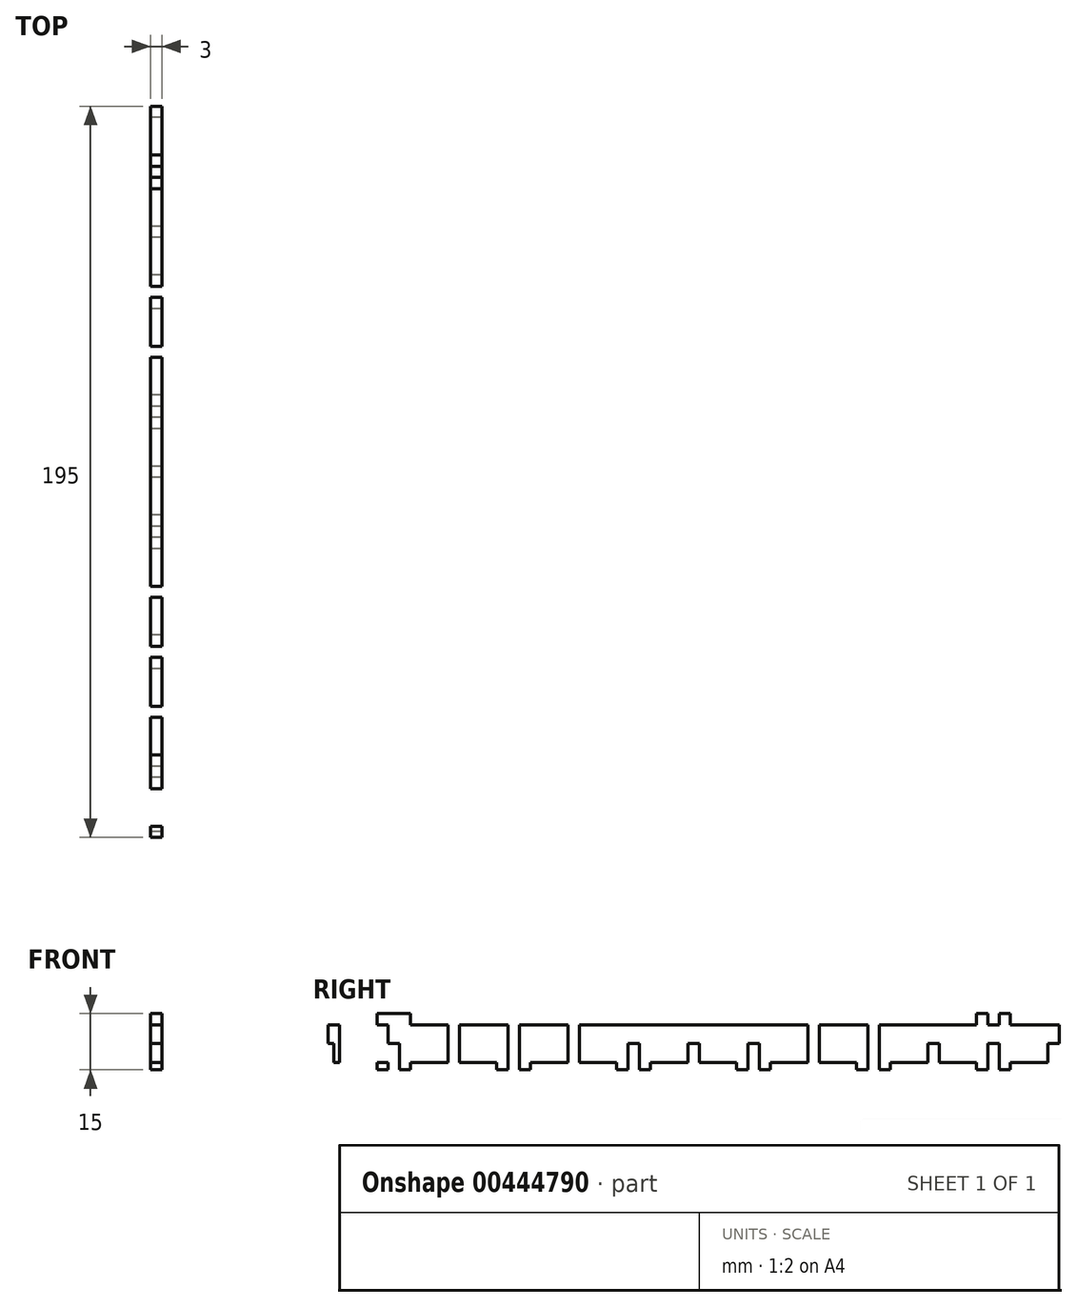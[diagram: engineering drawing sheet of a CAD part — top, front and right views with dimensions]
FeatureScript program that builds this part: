
annotation { "Feature Type Name" : "Feature", "Feature Type Description" : "" }
export const myFeature = defineFeature(function(context is Context, id is Id, definition is map)
    precondition{}
    {
        {
            var Q0;
            Q0=qCreatedBy(makeId("Right.planeOp"),FACE);
            var sketch = newSketch(context, id + "F0", { "sketchPlane" : qUnion([Q0])});
            skLineSegment(sketch, "E0", {"start": v(0, 0) * mm, "end": v(11.5, 0) * mm});
            skLineSegment(sketch, "E1", {"start": v(11.5, 0) * mm, "end": v(11.5, -2) * mm});
            skLineSegment(sketch, "E2", {"start": v(11.5, -2) * mm, "end": v(20.5, -2) * mm});
            skLineSegment(sketch, "E3", {"start": v(20.5, -2) * mm, "end": v(20.5, 0) * mm});
            skLineSegment(sketch, "E4", {"start": v(20.5, 0) * mm, "end": v(43.5, 0) * mm});
            skLineSegment(sketch, "E5", {"start": v(43.5, 0) * mm, "end": v(43.5, -2) * mm});
            skLineSegment(sketch, "E6", {"start": v(43.5, -2) * mm, "end": v(52.5, -2) * mm});
            skLineSegment(sketch, "E7", {"start": v(52.5, -2) * mm, "end": v(52.5, 0) * mm});
            skLineSegment(sketch, "E8", {"start": v(0, 0) * mm, "end": v(0, 10) * mm});
            skPoint(sketch, "E9.oppositeSnap0", {"position": v(0, 5) * mm});
            skLineSegment(sketch, "E9.bottom", {"start": v(0, 10) * mm, "end": v(-1.5, 10) * mm});
            skLineSegment(sketch, "E9.top", {"start": v(0, 5) * mm, "end": v(-1.5, 5) * mm});
            skLineSegment(sketch, "E9.left", {"start": v(0, 10) * mm, "end": v(0, 5) * mm});
            skLineSegment(sketch, "E9.right", {"start": v(-1.5, 10) * mm, "end": v(-1.5, 5) * mm});
            skLineSegment(sketch, "E10.bottom", {"start": v(14.5, 10) * mm, "end": v(17.5, 10) * mm});
            skLineSegment(sketch, "E10.top", {"start": v(14.5, 5) * mm, "end": v(17.5, 5) * mm});
            skLineSegment(sketch, "E10.left", {"start": v(14.5, 10) * mm, "end": v(14.5, 5) * mm});
            skLineSegment(sketch, "E10.right", {"start": v(17.5, 10) * mm, "end": v(17.5, 5) * mm});
            skLineSegment(sketch, "E11.top", {"start": v(0, 0) * mm, "end": v(-1.5, 0) * mm});
            skLineSegment(sketch, "E11.left", {"start": v(0, 5) * mm, "end": v(0, 0) * mm});
            skLineSegment(sketch, "E11.right", {"start": v(-1.5, 5) * mm, "end": v(-1.5, 0) * mm});
            skLineSegment(sketch, "E12.top", {"start": v(14.5, -2) * mm, "end": v(17.5, -2) * mm});
            skLineSegment(sketch, "E12.left", {"start": v(14.5, 5) * mm, "end": v(14.5, -2) * mm});
            skLineSegment(sketch, "E12.right", {"start": v(17.5, 5) * mm, "end": v(17.5, -2) * mm});
            skLineSegment(sketch, "E13.bottom", {"start": v(0, 10) * mm, "end": v(1.5, 10) * mm});
            skLineSegment(sketch, "E13.top", {"start": v(0, 5) * mm, "end": v(1.5, 5) * mm});
            skLineSegment(sketch, "E13.right", {"start": v(1.5, 10) * mm, "end": v(1.5, 5) * mm});
            skLineSegment(sketch, "E14.top", {"start": v(0, 0) * mm, "end": v(1.5, 0) * mm});
            skLineSegment(sketch, "E14.right", {"start": v(1.5, 5) * mm, "end": v(1.5, 0) * mm});
            skLineSegment(sketch, "E15.bottom", {"start": v(11.5, 10) * mm, "end": v(20.5, 10) * mm});
            skLineSegment(sketch, "E15.top", {"start": v(11.5, 13) * mm, "end": v(20.5, 13) * mm});
            skLineSegment(sketch, "E15.left", {"start": v(11.5, 10) * mm, "end": v(11.5, 13) * mm});
            skLineSegment(sketch, "E15.right", {"start": v(20.5, 10) * mm, "end": v(20.5, 13) * mm});
            skLineSegment(sketch, "E16", {"start": v(52.5, 0) * mm, "end": v(75.5, 0) * mm});
            skLineSegment(sketch, "E17", {"start": v(75.5, 0) * mm, "end": v(75.5, -2) * mm});
            skLineSegment(sketch, "E18", {"start": v(75.5, -2) * mm, "end": v(84.5, -2) * mm});
            skLineSegment(sketch, "E19", {"start": v(84.5, -2) * mm, "end": v(84.5, 0) * mm});
            skLineSegment(sketch, "E20", {"start": v(84.5, 0) * mm, "end": v(96, 0) * mm});
            skLineSegment(sketch, "E21", {"start": v(96, 0) * mm, "end": v(96, 19.13) * mm, "construction": true});
            skLineSegment(sketch, "E22", {"start": v(16, 10) * mm, "end": v(16, 11.65) * mm, "construction": true});
            skLineSegment(sketch, "E23.bottom", {"start": v(30.5, 0) * mm, "end": v(33.5, 0) * mm});
            skLineSegment(sketch, "E23.top", {"start": v(30.5, 5) * mm, "end": v(33.5, 5) * mm});
            skLineSegment(sketch, "E23.left", {"start": v(30.5, 0) * mm, "end": v(30.5, 5) * mm});
            skLineSegment(sketch, "E23.right", {"start": v(33.5, 0) * mm, "end": v(33.5, 5) * mm});
            skLineSegment(sketch, "E24.bottom", {"start": v(33.5, 5) * mm, "end": v(30.5, 5) * mm});
            skLineSegment(sketch, "E24.top", {"start": v(33.5, 10) * mm, "end": v(30.5, 10) * mm});
            skLineSegment(sketch, "E24.left", {"start": v(33.5, 5) * mm, "end": v(33.5, 10) * mm});
            skLineSegment(sketch, "E24.right", {"start": v(30.5, 5) * mm, "end": v(30.5, 10) * mm});
            skLineSegment(sketch, "E25", {"start": v(32, 0) * mm, "end": v(32, 2.31) * mm, "construction": true});
            skLineSegment(sketch, "E26.bottom", {"start": v(46.5, -2) * mm, "end": v(49.5, -2) * mm});
            skLineSegment(sketch, "E26.top", {"start": v(46.5, 5) * mm, "end": v(49.5, 5) * mm});
            skLineSegment(sketch, "E26.left", {"start": v(46.5, -2) * mm, "end": v(46.5, 5) * mm});
            skLineSegment(sketch, "E26.right", {"start": v(49.5, -2) * mm, "end": v(49.5, 5) * mm});
            skLineSegment(sketch, "E27.bottom", {"start": v(49.5, 5) * mm, "end": v(46.5, 5) * mm});
            skLineSegment(sketch, "E27.top", {"start": v(49.5, 10) * mm, "end": v(46.5, 10) * mm});
            skLineSegment(sketch, "E27.left", {"start": v(49.5, 5) * mm, "end": v(49.5, 10) * mm});
            skLineSegment(sketch, "E27.right", {"start": v(46.5, 5) * mm, "end": v(46.5, 10) * mm});
            skLineSegment(sketch, "E28.bottom", {"start": v(62.5, 0) * mm, "end": v(65.5, 0) * mm});
            skLineSegment(sketch, "E28.top", {"start": v(62.5, 5) * mm, "end": v(65.5, 5) * mm});
            skLineSegment(sketch, "E28.left", {"start": v(62.5, 0) * mm, "end": v(62.5, 5) * mm});
            skLineSegment(sketch, "E28.right", {"start": v(65.5, 0) * mm, "end": v(65.5, 5) * mm});
            skLineSegment(sketch, "E29.bottom", {"start": v(65.5, 5) * mm, "end": v(62.5, 5) * mm});
            skLineSegment(sketch, "E29.top", {"start": v(65.5, 10) * mm, "end": v(62.5, 10) * mm});
            skLineSegment(sketch, "E29.left", {"start": v(65.5, 5) * mm, "end": v(65.5, 10) * mm});
            skLineSegment(sketch, "E29.right", {"start": v(62.5, 5) * mm, "end": v(62.5, 10) * mm});
            skLineSegment(sketch, "E30.bottom", {"start": v(81.5, -2) * mm, "end": v(78.5, -2) * mm});
            skLineSegment(sketch, "E30.top", {"start": v(81.5, 5) * mm, "end": v(78.5, 5) * mm});
            skLineSegment(sketch, "E30.left", {"start": v(81.5, -2) * mm, "end": v(81.5, 5) * mm});
            skLineSegment(sketch, "E30.right", {"start": v(78.5, -2) * mm, "end": v(78.5, 5) * mm});
            skLineSegment(sketch, "E31.top", {"start": v(81.5, 10) * mm, "end": v(78.5, 10) * mm});
            skLineSegment(sketch, "E31.left", {"start": v(81.5, 5) * mm, "end": v(81.5, 10) * mm});
            skLineSegment(sketch, "E31.right", {"start": v(78.5, 5) * mm, "end": v(78.5, 10) * mm});
            skLineSegment(sketch, "E32.bottom", {"start": v(96, 0) * mm, "end": v(94.5, 0) * mm});
            skLineSegment(sketch, "E32.top", {"start": v(96, 5) * mm, "end": v(94.5, 5) * mm});
            skLineSegment(sketch, "E32.left", {"start": v(96, 0) * mm, "end": v(96, 5) * mm});
            skLineSegment(sketch, "E32.right", {"start": v(94.5, 0) * mm, "end": v(94.5, 5) * mm});
            skLineSegment(sketch, "E33.left", {"start": v(96, 5) * mm, "end": v(96, 5) * mm});
            skLineSegment(sketch, "E33.right", {"start": v(94.5, 5) * mm, "end": v(94.5, 5) * mm});
            skLineSegment(sketch, "E34.top", {"start": v(96, 10) * mm, "end": v(94.5, 10) * mm});
            skLineSegment(sketch, "E34.left", {"start": v(96, 5) * mm, "end": v(96, 10) * mm});
            skLineSegment(sketch, "E34.right", {"start": v(94.5, 5) * mm, "end": v(94.5, 10) * mm});
            skLineSegment(sketch, "E35", {"start": v(48, -2) * mm, "end": v(48, 0) * mm, "construction": true});
            skLineSegment(sketch, "E36", {"start": v(64, 0) * mm, "end": v(64, 2.67) * mm, "construction": true});
            skLineSegment(sketch, "E37", {"start": v(80, -2) * mm, "end": v(80, 0) * mm, "construction": true});
            skLineSegment(sketch, "E38", {"start": v(1.5, 10) * mm, "end": v(96, 10) * mm});
            skLineSegment(sketch, "E39.MirrorCS", {"start": v(96, 5) * mm, "end": v(97.5, 5) * mm});
            skLineSegment(sketch, "E40.MirrorCS", {"start": v(145.5, 5) * mm, "end": v(142.5, 5) * mm});
            skLineSegment(sketch, "E41.MirrorCS", {"start": v(110.5, 5) * mm, "end": v(113.5, 5) * mm});
            skLineSegment(sketch, "E42.MirrorCS", {"start": v(129.5, 5) * mm, "end": v(126.5, 5) * mm});
            skLineSegment(sketch, "E43.MirrorCS", {"start": v(177.5, 5) * mm, "end": v(174.5, 5) * mm});
            skLineSegment(sketch, "E44.MirrorCS", {"start": v(192, 5) * mm, "end": v(190.5, 5) * mm});
            skLineSegment(sketch, "E45.MirrorCS", {"start": v(192, 5) * mm, "end": v(193.5, 5) * mm});
            skLineSegment(sketch, "E46.MirrorCS", {"start": v(142.5, 5) * mm, "end": v(145.5, 5) * mm});
            skLineSegment(sketch, "E47.MirrorCS", {"start": v(126.5, 5) * mm, "end": v(129.5, 5) * mm});
            skLineSegment(sketch, "E48.MirrorCS", {"start": v(192, 10) * mm, "end": v(190.5, 10) * mm});
            skLineSegment(sketch, "E49.MirrorCS", {"start": v(171.5, -2) * mm, "end": v(171.5, 0) * mm});
            skLineSegment(sketch, "E50.MirrorCS", {"start": v(180.5, 0) * mm, "end": v(180.5, -2) * mm});
            skLineSegment(sketch, "E51.MirrorCS", {"start": v(177.5, 10) * mm, "end": v(174.5, 10) * mm});
            skLineSegment(sketch, "E52.MirrorCS", {"start": v(116.5, 0) * mm, "end": v(116.5, -2) * mm});
            skLineSegment(sketch, "E53.MirrorCS", {"start": v(177.5, -2) * mm, "end": v(174.5, -2) * mm});
            skLineSegment(sketch, "E54.MirrorCS", {"start": v(192, 0) * mm, "end": v(190.5, 0) * mm});
            skLineSegment(sketch, "E55.MirrorCS", {"start": v(126.5, 10) * mm, "end": v(129.5, 10) * mm});
            skLineSegment(sketch, "E56.MirrorCS", {"start": v(145.5, -2) * mm, "end": v(142.5, -2) * mm});
            skLineSegment(sketch, "E57.MirrorCS", {"start": v(110.5, -2) * mm, "end": v(113.5, -2) * mm});
            skLineSegment(sketch, "E58.MirrorCS", {"start": v(192, 0) * mm, "end": v(193.5, 0) * mm});
            skLineSegment(sketch, "E59.MirrorCS", {"start": v(96, 10) * mm, "end": v(97.5, 10) * mm});
            skLineSegment(sketch, "E60.MirrorCS", {"start": v(110.5, 10) * mm, "end": v(113.5, 10) * mm});
            skLineSegment(sketch, "E61.MirrorCS", {"start": v(142.5, 10) * mm, "end": v(145.5, 10) * mm});
            skLineSegment(sketch, "E62.MirrorCS", {"start": v(107.5, -2) * mm, "end": v(107.5, 0) * mm});
            skLineSegment(sketch, "E63.MirrorCS", {"start": v(192, 10) * mm, "end": v(193.5, 10) * mm});
            skLineSegment(sketch, "E64.MirrorCS", {"start": v(96, 0) * mm, "end": v(97.5, 0) * mm});
            skLineSegment(sketch, "E65.MirrorCS", {"start": v(139.5, -2) * mm, "end": v(139.5, 0) * mm});
            skLineSegment(sketch, "E66.MirrorCS", {"start": v(129.5, 0) * mm, "end": v(126.5, 0) * mm});
            skLineSegment(sketch, "E67.MirrorCS", {"start": v(148.5, 0) * mm, "end": v(148.5, -2) * mm});
            skLineSegment(sketch, "E68.MirrorCS", {"start": v(192, 5) * mm, "end": v(192, 0) * mm});
            skLineSegment(sketch, "E69.MirrorCS", {"start": v(112, -2) * mm, "end": v(112, 0) * mm, "construction": true});
            skLineSegment(sketch, "E70.MirrorCS", {"start": v(176, 10) * mm, "end": v(176, 11.65) * mm, "construction": true});
            skLineSegment(sketch, "E71.MirrorCS", {"start": v(192, 10) * mm, "end": v(192, 5) * mm});
            skLineSegment(sketch, "E72.MirrorCS", {"start": v(161.5, 0) * mm, "end": v(158.5, 0) * mm});
            skLineSegment(sketch, "E73.MirrorCS", {"start": v(128, 0) * mm, "end": v(128, 2.67) * mm, "construction": true});
            skLineSegment(sketch, "E74.MirrorCS", {"start": v(160, 0) * mm, "end": v(160, 2.31) * mm, "construction": true});
            skLineSegment(sketch, "E75.MirrorCS", {"start": v(144, -2) * mm, "end": v(144, 0) * mm, "construction": true});
            skLineSegment(sketch, "E76.MirrorCS", {"start": v(161.5, 5) * mm, "end": v(158.5, 5) * mm});
            skLineSegment(sketch, "E77.MirrorCS", {"start": v(171.5, 0) * mm, "end": v(148.5, 0) * mm});
            skLineSegment(sketch, "E78.MirrorCS", {"start": v(180.5, -2) * mm, "end": v(171.5, -2) * mm});
            skLineSegment(sketch, "E79.MirrorCS", {"start": v(192, 0) * mm, "end": v(180.5, 0) * mm});
            skLineSegment(sketch, "E80.MirrorCS", {"start": v(177.5, 10) * mm, "end": v(177.5, 5) * mm});
            skLineSegment(sketch, "E81.MirrorCS", {"start": v(158.5, 0) * mm, "end": v(158.5, 5) * mm});
            skLineSegment(sketch, "E82.MirrorCS", {"start": v(129.5, 0) * mm, "end": v(129.5, 5) * mm});
            skLineSegment(sketch, "E83.MirrorCS", {"start": v(97.5, 5) * mm, "end": v(97.5, 10) * mm});
            skPoint(sketch, "E84.MirrorP", {"position": v(192, 5) * mm});
            skLineSegment(sketch, "E85.MirrorCS", {"start": v(139.5, 0) * mm, "end": v(116.5, 0) * mm});
            skLineSegment(sketch, "E86.MirrorCS", {"start": v(126.5, 5) * mm, "end": v(126.5, 10) * mm});
            skLineSegment(sketch, "E87.MirrorCS", {"start": v(161.5, 5) * mm, "end": v(161.5, 10) * mm});
            skLineSegment(sketch, "E88.MirrorCS", {"start": v(180.5, 10) * mm, "end": v(180.5, 13) * mm});
            skLineSegment(sketch, "E89.MirrorCS", {"start": v(180.5, 13) * mm, "end": v(171.5, 13) * mm});
            skLineSegment(sketch, "E90.MirrorCS", {"start": v(158.5, 5) * mm, "end": v(158.5, 10) * mm});
            skLineSegment(sketch, "E91.MirrorCS", {"start": v(161.5, 0) * mm, "end": v(161.5, 5) * mm});
            skLineSegment(sketch, "E92.MirrorCS", {"start": v(107.5, 0) * mm, "end": v(96, 0) * mm});
            skLineSegment(sketch, "E93.MirrorCS", {"start": v(142.5, 5) * mm, "end": v(142.5, 10) * mm});
            skLineSegment(sketch, "E94.MirrorCS", {"start": v(193.5, 5) * mm, "end": v(193.5, 0) * mm});
            skLineSegment(sketch, "E95.MirrorCS", {"start": v(110.5, 5) * mm, "end": v(110.5, 10) * mm});
            skLineSegment(sketch, "E96.MirrorCS", {"start": v(180.5, 10) * mm, "end": v(171.5, 10) * mm});
            skLineSegment(sketch, "E97.MirrorCS", {"start": v(158.5, 10) * mm, "end": v(161.5, 10) * mm});
            skLineSegment(sketch, "E98.MirrorCS", {"start": v(145.5, 5) * mm, "end": v(145.5, 10) * mm});
            skLineSegment(sketch, "E99.MirrorCS", {"start": v(113.5, -2) * mm, "end": v(113.5, 5) * mm});
            skLineSegment(sketch, "E100.MirrorCS", {"start": v(174.5, 5) * mm, "end": v(174.5, -2) * mm});
            skLineSegment(sketch, "E101.MirrorCS", {"start": v(142.5, -2) * mm, "end": v(142.5, 5) * mm});
            skLineSegment(sketch, "E102.MirrorCS", {"start": v(113.5, 5) * mm, "end": v(113.5, 10) * mm});
            skLineSegment(sketch, "E103.MirrorCS", {"start": v(190.5, 10) * mm, "end": v(96, 10) * mm});
            skLineSegment(sketch, "E104.MirrorCS", {"start": v(190.5, 5) * mm, "end": v(190.5, 0) * mm});
            skLineSegment(sketch, "E105.MirrorCS", {"start": v(158.5, 5) * mm, "end": v(161.5, 5) * mm});
            skLineSegment(sketch, "E106.MirrorCS", {"start": v(126.5, 0) * mm, "end": v(126.5, 5) * mm});
            skLineSegment(sketch, "E107.MirrorCS", {"start": v(97.5, 0) * mm, "end": v(97.5, 5) * mm});
            skLineSegment(sketch, "E108.MirrorCS", {"start": v(174.5, 10) * mm, "end": v(174.5, 5) * mm});
            skLineSegment(sketch, "E109.MirrorCS", {"start": v(110.5, -2) * mm, "end": v(110.5, 5) * mm});
            skLineSegment(sketch, "E110.MirrorCS", {"start": v(177.5, 5) * mm, "end": v(177.5, -2) * mm});
            skLineSegment(sketch, "E111.MirrorCS", {"start": v(116.5, -2) * mm, "end": v(107.5, -2) * mm});
            skLineSegment(sketch, "E112.MirrorCS", {"start": v(145.5, -2) * mm, "end": v(145.5, 5) * mm});
            skLineSegment(sketch, "E113.MirrorCS", {"start": v(193.5, 10) * mm, "end": v(193.5, 5) * mm});
            skLineSegment(sketch, "E114.MirrorCS", {"start": v(129.5, 5) * mm, "end": v(129.5, 10) * mm});
            skLineSegment(sketch, "E115.MirrorCS", {"start": v(192, 0) * mm, "end": v(192, 10) * mm});
            skLineSegment(sketch, "E116.MirrorCS", {"start": v(148.5, -2) * mm, "end": v(139.5, -2) * mm});
            skLineSegment(sketch, "E117.MirrorCS", {"start": v(171.5, 10) * mm, "end": v(171.5, 13) * mm});
            skLineSegment(sketch, "E118.MirrorCS", {"start": v(190.5, 10) * mm, "end": v(190.5, 5) * mm});
            skLineSegment(sketch, "E119.top", {"start": v(14.5, 13) * mm, "end": v(17.5, 13) * mm});
            skLineSegment(sketch, "E119.left", {"start": v(14.5, 10) * mm, "end": v(14.5, 13) * mm});
            skLineSegment(sketch, "E119.right", {"start": v(17.5, 10) * mm, "end": v(17.5, 13) * mm});
            skLineSegment(sketch, "E120.bottom", {"start": v(174.5, 10) * mm, "end": v(177.5, 10) * mm});
            skLineSegment(sketch, "E120.top", {"start": v(174.5, 13) * mm, "end": v(177.5, 13) * mm});
            skLineSegment(sketch, "E120.left", {"start": v(174.5, 10) * mm, "end": v(174.5, 13) * mm});
            skLineSegment(sketch, "E120.right", {"start": v(177.5, 10) * mm, "end": v(177.5, 13) * mm});
            skLineSegment(sketch, "E121", {"start": v(11.5, 0) * mm, "end": v(180.5, 0) * mm});
            skSolve(sketch);
        }
        {
            var Q0;
            Q0=makeQuery(id+"F0.imprint","IMPRINT",FACE,{"disambiguationData":[TD([[makeQuery(id+"F0.imprint","IMPRINT",EDGE,{"derivedFrom":sQuery(id+"F0.wireOp",EDGE,"E0")}),1.0]])]});
            var Q1;
            Q1=makeQuery(id+"F0.imprint","IMPRINT",FACE,{"disambiguationData":[TD([[makeQuery(id+"F0.imprint","IMPRINT",EDGE,{"derivedFrom":sQuery(id+"F0.wireOp",EDGE,"E10.bottom")}),-1.0]])]});
            var Q2;
            {var subQ1=sQuery(id+"F0.wireOp",EDGE,"E10.right");Q2=makeQuery(id+"F0.imprint","IMPRINT",FACE,{"disambiguationData":[TD([[makeQuery(id+"F0.imprint","IMPRINT",EDGE,{"derivedFrom":subQ1}),1.0]])]});}
            var Q3;
            Q3=makeQuery(id+"F0.imprint","IMPRINT",FACE,{"disambiguationData":[TD([[makeQuery(id+"F0.imprint","IMPRINT",EDGE,{"derivedFrom":sQuery(id+"F0.wireOp",EDGE,"exBxU9Mq-clvg-588H-Zr5o-6X85DIsckNDc.bottom")}),1.0]])]});
            var Q4;
            {var subQ4=sQuery(id+"F0.wireOp",EDGE,"E5");Q4=makeQuery(id+"F0.imprint","IMPRINT",FACE,{"disambiguationData":[TD([[makeQuery(id+"F0.imprint","IMPRINT",EDGE,{"derivedFrom":subQ4}),1.0]])]});}
            var Q5;
            Q5=makeQuery(id+"F0.imprint","IMPRINT",FACE,{"disambiguationData":[TD([[makeQuery(id+"F0.imprint","IMPRINT",EDGE,{"derivedFrom":sQuery(id+"F0.wireOp",EDGE,"AYazpiCl-vhh2-3qVq-SwRU-viVl95edflrx.bottom")}),-1.0]])]});
            var Q6;
            {var subQ0=sQuery(id+"F0.wireOp",EDGE,"AYazpiCl-vhh2-3qVq-SwRU-viVl95edflrx.right");Q6=makeQuery(id+"F0.imprint","IMPRINT",FACE,{"disambiguationData":[TD([[makeQuery(id+"F0.imprint","IMPRINT",EDGE,{"derivedFrom":subQ0}),1.0]])]});}
            var Q7;
            Q7=makeQuery(id+"F0.imprint","IMPRINT",FACE,{"disambiguationData":[TD([[makeQuery(id+"F0.imprint","IMPRINT",EDGE,{"derivedFrom":sQuery(id+"F0.wireOp",EDGE,"4bEUlQAV-gPeH-rYiX-vIa2-gnOWGRHJXyY5.bottom")}),-1.0]])]});
            var Q8;
            Q8=makeQuery(id+"F0.imprint","IMPRINT",FACE,{"disambiguationData":[TD([[makeQuery(id+"F0.imprint","IMPRINT",EDGE,{"derivedFrom":sQuery(id+"F0.wireOp",EDGE,"73e3d719-c9b8-4955-bdff-4b6c16a5061d.1.0.2")}),1.0]])]});
            var Q9;
            Q9=makeQuery(id+"F0.imprint","IMPRINT",FACE,{"disambiguationData":[TD([[makeQuery(id+"F0.imprint","IMPRINT",EDGE,{"derivedFrom":sQuery(id+"F0.wireOp",EDGE,"RX1Oao4A-lbR6-l0fM-smuL-DuWmTi57Jbgw.bottom")}),-1.0]])]});
            var Q10;
            {var subQ2=sQuery(id+"F0.wireOp",EDGE,"RX1Oao4A-lbR6-l0fM-smuL-DuWmTi57Jbgw.right");Q10=makeQuery(id+"F0.imprint","IMPRINT",FACE,{"disambiguationData":[TD([[makeQuery(id+"F0.imprint","IMPRINT",EDGE,{"derivedFrom":subQ2}),1.0]])]});}
            var Q11;
            Q11=makeQuery(id+"F0.imprint","IMPRINT",FACE,{"disambiguationData":[TD([[makeQuery(id+"F0.imprint","IMPRINT",EDGE,{"derivedFrom":sQuery(id+"F0.wireOp",EDGE,"lx0Yxyhi-8TGn-ab6C-Jwk7-24dBiMFvEcRQ.bottom")}),1.0]])]});
            var Q12;
            Q12=makeQuery(id+"F0.imprint","IMPRINT",FACE,{"disambiguationData":[TD([[makeQuery(id+"F0.imprint","IMPRINT",EDGE,{"derivedFrom":sQuery(id+"F0.wireOp",EDGE,"73e3d719-c9b8-4955-bdff-4b6c16a5061d.2.0.2")}),1.0]])]});
            var Q13;
            Q13=makeQuery(id+"F0.imprint","IMPRINT",FACE,{"disambiguationData":[TD([[makeQuery(id+"F0.imprint","IMPRINT",EDGE,{"derivedFrom":sQuery(id+"F0.wireOp",EDGE,"l3f9ZwhA-5mlz-sbFQ-bDJ1-22Tfedz6XSHV.bottom")}),-1.0]])]});
            var Q14;
            {var subQ1=sQuery(id+"F0.wireOp",EDGE,"l3f9ZwhA-5mlz-sbFQ-bDJ1-22Tfedz6XSHV.right");Q14=makeQuery(id+"F0.imprint","IMPRINT",FACE,{"disambiguationData":[TD([[makeQuery(id+"F0.imprint","IMPRINT",EDGE,{"derivedFrom":subQ1}),1.0]])]});}
            var Q15;
            Q15=makeQuery(id+"F0.imprint","IMPRINT",FACE,{"disambiguationData":[TD([[makeQuery(id+"F0.imprint","IMPRINT",EDGE,{"derivedFrom":sQuery(id+"F0.wireOp",EDGE,"wGrJq75p-ImmZ-GG0w-oumq-Kc8NIA52VM4L.bottom")}),1.0]])]});
            var Q16;
            Q16=makeQuery(id+"F0.imprint","IMPRINT",FACE,{"disambiguationData":[TD([[makeQuery(id+"F0.imprint","IMPRINT",EDGE,{"derivedFrom":sQuery(id+"F0.wireOp",EDGE,"73e3d719-c9b8-4955-bdff-4b6c16a5061d.3.0.2")}),1.0]])]});
            var Q17;
            Q17=makeQuery(id+"F0.imprint","IMPRINT",FACE,{"disambiguationData":[TD([[makeQuery(id+"F0.imprint","IMPRINT",EDGE,{"derivedFrom":sQuery(id+"F0.wireOp",EDGE,"E13.bottom")}),-1.0]])]});
            var Q18;
            Q18=makeQuery(id+"F0.imprint","IMPRINT",FACE,{"disambiguationData":[TD([[makeQuery(id+"F0.imprint","IMPRINT",EDGE,{"derivedFrom":sQuery(id+"F0.wireOp",EDGE,"SeUBRtC9-CtK3-iZ4W-e8DI-C3XoFjQM9IDC.bottom")}),1.0]])]});
            var Q19;
            Q19=makeQuery(id+"F0.imprint","IMPRINT",FACE,{"disambiguationData":[TD([[makeQuery(id+"F0.imprint","IMPRINT",EDGE,{"derivedFrom":sQuery(id+"F0.wireOp",EDGE,"RVkCzXDl-vvve-KC9k-oys3-LpA8b4wrY5XK.bottom")}),-1.0]])]});
            var Q20;
            Q20=makeQuery(id+"F0.imprint","IMPRINT",FACE,{"disambiguationData":[TD([[makeQuery(id+"F0.imprint","IMPRINT",EDGE,{"derivedFrom":sQuery(id+"F0.wireOp",EDGE,"E9.bottom")}),1.0]])]});
            var Q21;
            {var subQ0=sQuery(id+"F0.wireOp",EDGE,"wGrJq75p-ImmZ-GG0w-oumq-Kc8NIA52VM4L.left");Q21=makeQuery(id+"F0.imprint","IMPRINT",FACE,{"disambiguationData":[TD([[makeQuery(id+"F0.imprint","IMPRINT",EDGE,{"derivedFrom":subQ0}),-1.0]])]});}
            var Q22;
            {var subQ0=sQuery(id+"F0.wireOp",EDGE,"E10.left");Q22=makeQuery(id+"F0.imprint","IMPRINT",FACE,{"disambiguationData":[TD([[makeQuery(id+"F0.imprint","IMPRINT",EDGE,{"derivedFrom":subQ0}),1.0]])]});}
            var Q23;
            Q23=makeQuery(id+"F0.imprint","IMPRINT",FACE,{"disambiguationData":[TD([[makeQuery(id+"F0.imprint","IMPRINT",EDGE,{"derivedFrom":sQuery(id+"F0.wireOp",EDGE,"E15.top")}),-1.0]])]});
            var Q24;
            Q24=makeQuery(id+"F0.imprint","IMPRINT",FACE,{"disambiguationData":[TD([[makeQuery(id+"F0.imprint","IMPRINT",EDGE,{"derivedFrom":sQuery(id+"F0.wireOp",EDGE,"E24.bottom")}),-1.0]])]});
            var Q25;
            Q25=makeQuery(id+"F0.imprint","IMPRINT",FACE,{"disambiguationData":[TD([[makeQuery(id+"F0.imprint","IMPRINT",EDGE,{"derivedFrom":sQuery(id+"F0.wireOp",EDGE,"E27.bottom")}),-1.0]])]});
            var Q26;
            {var subQ2=sQuery(id+"F0.wireOp",EDGE,"E7");Q26=makeQuery(id+"F0.imprint","IMPRINT",FACE,{"disambiguationData":[TD([[makeQuery(id+"F0.imprint","IMPRINT",EDGE,{"derivedFrom":subQ2}),1.0]])]});}
            var Q27;
            Q27=makeQuery(id+"F0.imprint","IMPRINT",FACE,{"disambiguationData":[TD([[makeQuery(id+"F0.imprint","IMPRINT",EDGE,{"derivedFrom":sQuery(id+"F0.wireOp",EDGE,"E29.bottom")}),-1.0]])]});
            var Q28;
            {var subQ1=sQuery(id+"F0.wireOp",EDGE,"E17");Q28=makeQuery(id+"F0.imprint","IMPRINT",FACE,{"disambiguationData":[TD([[makeQuery(id+"F0.imprint","IMPRINT",EDGE,{"derivedFrom":subQ1}),1.0]])]});}
            var Q29;
            Q29=makeQuery(id+"F0.imprint","IMPRINT",FACE,{"disambiguationData":[TD([[makeQuery(id+"F0.imprint","IMPRINT",EDGE,{"derivedFrom":sQuery(id+"F0.wireOp",EDGE,"E30.top")}),-1.0]])]});
            var Q30;
            {var subQ1=sQuery(id+"F0.wireOp",EDGE,"E19");Q30=makeQuery(id+"F0.imprint","IMPRINT",FACE,{"disambiguationData":[TD([[makeQuery(id+"F0.imprint","IMPRINT",EDGE,{"derivedFrom":subQ1}),1.0]])]});}
            var Q31;
            Q31=makeQuery(id+"F0.imprint","IMPRINT",FACE,{"disambiguationData":[TD([[makeQuery(id+"F0.imprint","IMPRINT",EDGE,{"derivedFrom":sQuery(id+"F0.wireOp",EDGE,"E32.top")}),-1.0]])]});
            var Q32;
            Q32=makeQuery(id+"F0.imprint","IMPRINT",FACE,{"disambiguationData":[TD([[makeQuery(id+"F0.imprint","IMPRINT",EDGE,{"derivedFrom":sQuery(id+"F0.wireOp",EDGE,"E39.MirrorCS")}),1.0]])]});
            var Q33;
            {var subQ2=sQuery(id+"F0.wireOp",EDGE,"E62.MirrorCS");Q33=makeQuery(id+"F0.imprint","IMPRINT",FACE,{"disambiguationData":[TD([[makeQuery(id+"F0.imprint","IMPRINT",EDGE,{"derivedFrom":subQ2}),-1.0]])]});}
            var Q34;
            Q34=makeQuery(id+"F0.imprint","IMPRINT",FACE,{"disambiguationData":[TD([[makeQuery(id+"F0.imprint","IMPRINT",EDGE,{"derivedFrom":sQuery(id+"F0.wireOp",EDGE,"E41.MirrorCS")}),1.0]])]});
            var Q35;
            {var subQ2=sQuery(id+"F0.wireOp",EDGE,"E52.MirrorCS");Q35=makeQuery(id+"F0.imprint","IMPRINT",FACE,{"disambiguationData":[TD([[makeQuery(id+"F0.imprint","IMPRINT",EDGE,{"derivedFrom":subQ2}),-1.0]])]});}
            var Q36;
            Q36=makeQuery(id+"F0.imprint","IMPRINT",FACE,{"disambiguationData":[TD([[makeQuery(id+"F0.imprint","IMPRINT",EDGE,{"derivedFrom":sQuery(id+"F0.wireOp",EDGE,"E47.MirrorCS")}),1.0]])]});
            var Q37;
            {var subQ2=sQuery(id+"F0.wireOp",EDGE,"E65.MirrorCS");Q37=makeQuery(id+"F0.imprint","IMPRINT",FACE,{"disambiguationData":[TD([[makeQuery(id+"F0.imprint","IMPRINT",EDGE,{"derivedFrom":subQ2}),-1.0]])]});}
            var Q38;
            Q38=makeQuery(id+"F0.imprint","IMPRINT",FACE,{"disambiguationData":[TD([[makeQuery(id+"F0.imprint","IMPRINT",EDGE,{"derivedFrom":sQuery(id+"F0.wireOp",EDGE,"E46.MirrorCS")}),1.0]])]});
            var Q39;
            {var subQ1=sQuery(id+"F0.wireOp",EDGE,"E67.MirrorCS");Q39=makeQuery(id+"F0.imprint","IMPRINT",FACE,{"disambiguationData":[TD([[makeQuery(id+"F0.imprint","IMPRINT",EDGE,{"derivedFrom":subQ1}),-1.0]])]});}
            var Q40;
            {var subQ0=sQuery(id+"F0.wireOp",EDGE,"E87.MirrorCS");Q40=makeQuery(id+"F0.imprint","IMPRINT",FACE,{"disambiguationData":[TD([[makeQuery(id+"F0.imprint","IMPRINT",EDGE,{"derivedFrom":subQ0}),1.0]])]});}
            var Q41;
            {var subQ2=sQuery(id+"F0.wireOp",EDGE,"E49.MirrorCS");Q41=makeQuery(id+"F0.imprint","IMPRINT",FACE,{"disambiguationData":[TD([[makeQuery(id+"F0.imprint","IMPRINT",EDGE,{"derivedFrom":subQ2}),-1.0]])]});}
            var Q42;
            Q42=makeQuery(id+"F0.imprint","IMPRINT",FACE,{"disambiguationData":[TD([[makeQuery(id+"F0.imprint","IMPRINT",EDGE,{"derivedFrom":sQuery(id+"F0.wireOp",EDGE,"E43.MirrorCS")}),-1.0]])]});
            var Q43;
            {var subQ1=sQuery(id+"F0.wireOp",EDGE,"E50.MirrorCS");Q43=makeQuery(id+"F0.imprint","IMPRINT",FACE,{"disambiguationData":[TD([[makeQuery(id+"F0.imprint","IMPRINT",EDGE,{"derivedFrom":subQ1}),-1.0]])]});}
            var Q44;
            {var subQ0=sQuery(id+"F0.wireOp",EDGE,"E44.MirrorCS");Q44=makeQuery(id+"F0.imprint","IMPRINT",FACE,{"disambiguationData":[TD([[makeQuery(id+"F0.imprint","IMPRINT",EDGE,{"derivedFrom":subQ0}),-1.0]])]});}
            var Q45;
            {var subQ0=sQuery(id+"F0.wireOp",EDGE,"E45.MirrorCS");Q45=makeQuery(id+"F0.imprint","IMPRINT",FACE,{"disambiguationData":[TD([[makeQuery(id+"F0.imprint","IMPRINT",EDGE,{"derivedFrom":subQ0}),1.0]])]});}
            var Q46;
            {var subQ3=sQuery(id+"F0.wireOp",EDGE,"E88.MirrorCS");Q46=makeQuery(id+"F0.imprint","IMPRINT",FACE,{"disambiguationData":[TD([[makeQuery(id+"F0.imprint","IMPRINT",EDGE,{"derivedFrom":subQ3}),1.0]])]});}
            var Q47;
            Q47=makeQuery(id+"F0.imprint","IMPRINT",FACE,{"disambiguationData":[TD([[makeQuery(id+"F0.imprint","IMPRINT",EDGE,{"derivedFrom":sQuery(id+"F0.wireOp",EDGE,"E10.bottom")}),1.0]])]});
            var Q48;
            {var subQ0=sQuery(id+"F0.wireOp",EDGE,"E117.MirrorCS");Q48=makeQuery(id+"F0.imprint","IMPRINT",FACE,{"disambiguationData":[TD([[makeQuery(id+"F0.imprint","IMPRINT",EDGE,{"derivedFrom":subQ0}),-1.0]])]});}
            var Q49;
            Q49=makeQuery(id+"F0.imprint","IMPRINT",FACE,{"disambiguationData":[TD([[makeQuery(id+"F0.imprint","IMPRINT",EDGE,{"derivedFrom":sQuery(id+"F0.wireOp",EDGE,"E120.bottom")}),1.0]])]});
            var Q50;
            {var subQ0=sQuery(id+"F0.wireOp",EDGE,"E1");Q50=makeQuery(id+"F0.imprint","IMPRINT",FACE,{"disambiguationData":[TD([[makeQuery(id+"F0.imprint","IMPRINT",EDGE,{"derivedFrom":subQ0}),1.0]])]});}
            var Q51;
            {var subQ0=sQuery(id+"F0.wireOp",EDGE,"E3");Q51=makeQuery(id+"F0.imprint","IMPRINT",FACE,{"disambiguationData":[TD([[makeQuery(id+"F0.imprint","IMPRINT",EDGE,{"derivedFrom":subQ0}),1.0]])]});}
            var Q52;
            {var subQ1=sQuery(id+"F0.wireOp",EDGE,"E23.right");Q52=makeQuery(id+"F0.imprint","IMPRINT",FACE,{"disambiguationData":[TD([[makeQuery(id+"F0.imprint","IMPRINT",EDGE,{"derivedFrom":subQ1}),-1.0]])]});}
            var Q53;
            {var subQ2=sQuery(id+"F0.wireOp",EDGE,"E27.left");Q53=makeQuery(id+"F0.imprint","IMPRINT",FACE,{"disambiguationData":[TD([[makeQuery(id+"F0.imprint","IMPRINT",EDGE,{"derivedFrom":subQ2}),-1.0]])]});}
            var Q54;
            {var subQ1=sQuery(id+"F0.wireOp",EDGE,"E28.right");Q54=makeQuery(id+"F0.imprint","IMPRINT",FACE,{"disambiguationData":[TD([[makeQuery(id+"F0.imprint","IMPRINT",EDGE,{"derivedFrom":subQ1}),-1.0]])]});}
            var Q55;
            {var subQ2=sQuery(id+"F0.wireOp",EDGE,"E31.left");Q55=makeQuery(id+"F0.imprint","IMPRINT",FACE,{"disambiguationData":[TD([[makeQuery(id+"F0.imprint","IMPRINT",EDGE,{"derivedFrom":subQ2}),-1.0]])]});}
            var Q56;
            {var subQ2=sQuery(id+"F0.wireOp",EDGE,"E83.MirrorCS");Q56=makeQuery(id+"F0.imprint","IMPRINT",FACE,{"disambiguationData":[TD([[makeQuery(id+"F0.imprint","IMPRINT",EDGE,{"derivedFrom":subQ2}),-1.0]])]});}
            var Q57;
            {var subQ1=sQuery(id+"F0.wireOp",EDGE,"E86.MirrorCS");Q57=makeQuery(id+"F0.imprint","IMPRINT",FACE,{"disambiguationData":[TD([[makeQuery(id+"F0.imprint","IMPRINT",EDGE,{"derivedFrom":subQ1}),1.0]])]});}
            var Q58;
            {var subQ6=sQuery(id+"F0.wireOp",EDGE,"E82.MirrorCS");Q58=makeQuery(id+"F0.imprint","IMPRINT",FACE,{"disambiguationData":[TD([[makeQuery(id+"F0.imprint","IMPRINT",EDGE,{"derivedFrom":subQ6}),-1.0]])]});}
            var Q59;
            {var subQ7=sQuery(id+"F0.wireOp",EDGE,"E81.MirrorCS");Q59=makeQuery(id+"F0.imprint","IMPRINT",FACE,{"disambiguationData":[TD([[makeQuery(id+"F0.imprint","IMPRINT",EDGE,{"derivedFrom":subQ7}),1.0]])]});}
            var Q60;
            {var subQ7=sQuery(id+"F0.wireOp",EDGE,"E87.MirrorCS");Q60=makeQuery(id+"F0.imprint","IMPRINT",FACE,{"disambiguationData":[TD([[makeQuery(id+"F0.imprint","IMPRINT",EDGE,{"derivedFrom":subQ7}),-1.0]])]});}
            var Q61;
            {var subQ1=sQuery(id+"F0.wireOp",EDGE,"E80.MirrorCS");Q61=makeQuery(id+"F0.imprint","IMPRINT",FACE,{"disambiguationData":[TD([[makeQuery(id+"F0.imprint","IMPRINT",EDGE,{"derivedFrom":subQ1}),1.0]])]});}
            extrude(context, id + "F1", {"entities" : qUnion([Q0, Q1, Q2, Q3, Q4, Q5, Q6, Q7, Q8, Q9, Q10, Q11, Q12, Q13, Q14, Q15, Q16, Q17, Q18, Q19, Q20, Q21, Q22, Q23, Q24, Q25, Q26, Q27, Q28, Q29, Q30, Q31, Q32, Q33, Q34, Q35, Q36, Q37, Q38, Q39, Q40, Q41, Q42, Q43, Q44, Q45, Q46, Q47, Q48, Q49, Q50, Q51, Q52, Q53, Q54, Q55, Q56, Q57, Q58, Q59, Q60, Q61]), "depth" : 3 * mm});
        }
    });
